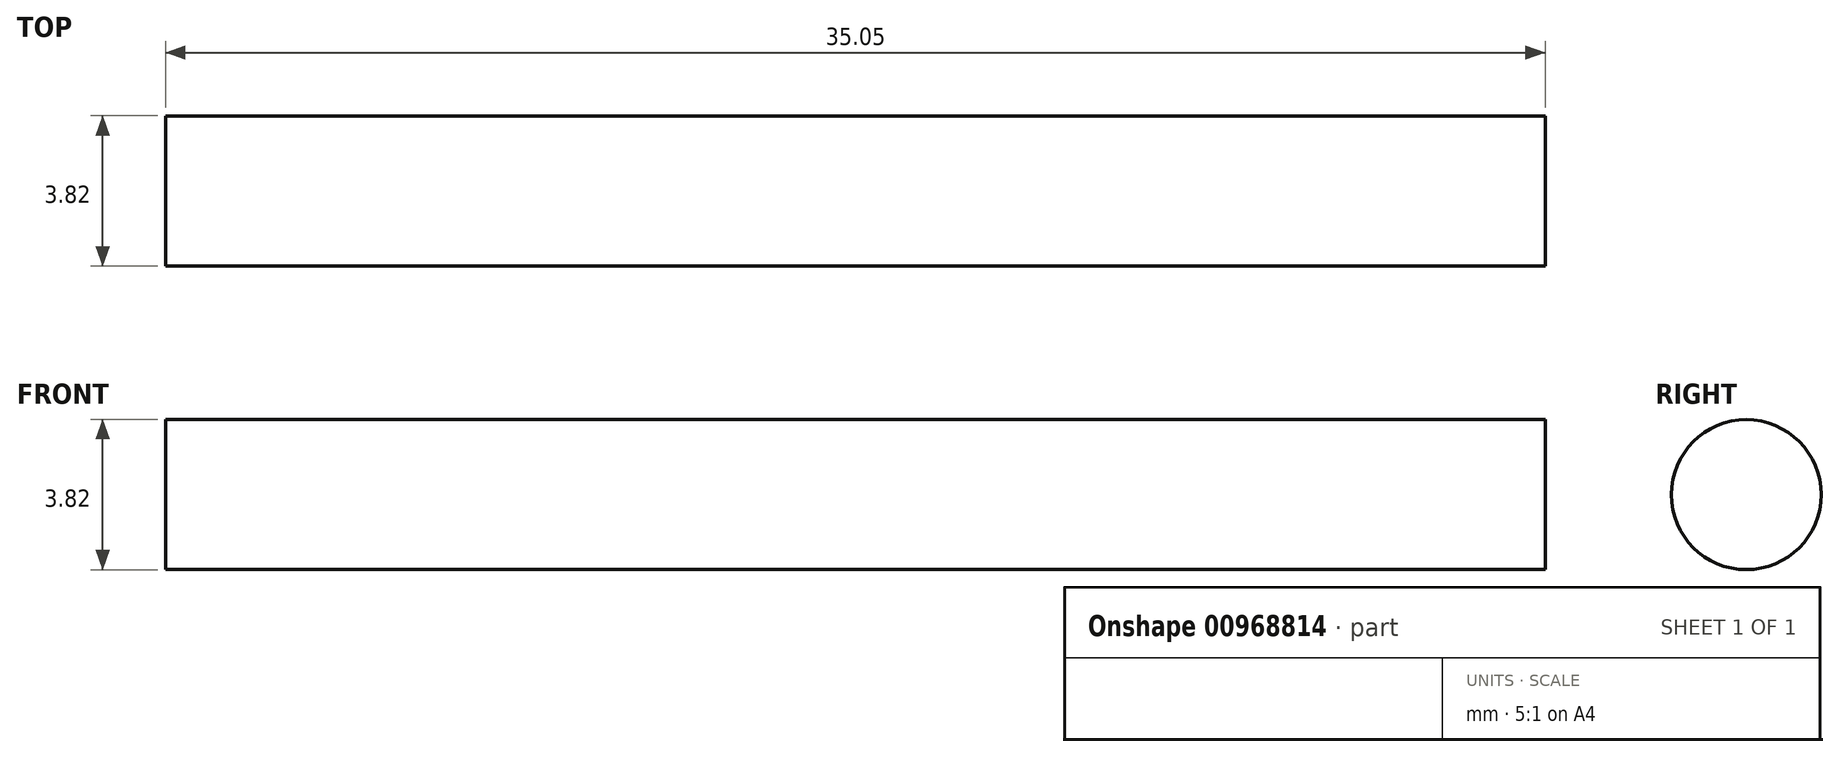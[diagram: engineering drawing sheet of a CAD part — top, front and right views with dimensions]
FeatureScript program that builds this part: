
annotation { "Feature Type Name" : "Feature", "Feature Type Description" : "" }
export const myFeature = defineFeature(function(context is Context, id is Id, definition is map)
    precondition{}
    {
        {
            var Q0;
            Q0=qCreatedBy(makeId("Right.planeOp"),FACE);
            var sketch = newSketch(context, id + "F0", { "sketchPlane" : qUnion([Q0])});
            skCircle(sketch, "E0", {"center": v(0, 0) * mm, "radius": 1.9 * mm});
            skSolve(sketch);
        }
        {
            var Q0;
            Q0 = qSketchRegion(id + "F0", true);
            extrude(context, id + "F1", {"entities" : qUnion([Q0]), "depth" : 35.05 * mm, "offsetDistance" : 25.4 * mm});
        }
    });
